# Revit family: C_66L_2DO_CAD_MULT_Prod
name_source: partatom
category: Detail Items
revit_build: Autodesk Revit 2015 (Build: 20140606_1530(x64)
units: mm (PartAtom-declared; Revit-internal decimal feet)

## types (4) — shared parameters
Density = 0.33 kg
Description = Nail plate
EPD = https://www.strongtie.eu
ETA / DoP = https://www.strongtie.eu
Manufacturer = Simpson Strong-Tie
Model = 66L
Model Disclaimer = Contact Simpson Strong-Tie Company  for more information
Model ID = 0283616690370330393471061069183467104661
Name = 66L
ObjectType = 66L
Product Material = Galvanised
Product Type = Nail plate
Reference = 66L
Technical datasheet = https://www.strongtie.eu
URL = www.strongtie.eu
UniClass Number = Pr_20_85_09_52
UniClass Title = Metal timber member fixing brackets

## per-type parameters (varying)
| type | _visiblefront | _visibleleft | _visibleright | _visibletop |
| SST_66L_Front | Yes | No | No | No |
| SST_66L_Top | No | No | No | Yes |
| SST_66L_Left | No | Yes | No | No |
| SST_66L_Right | No | No | Yes | No |

## geometry (parser evidence)
native form markers: Sweep x2
no freeform markers — native parametric forms only
